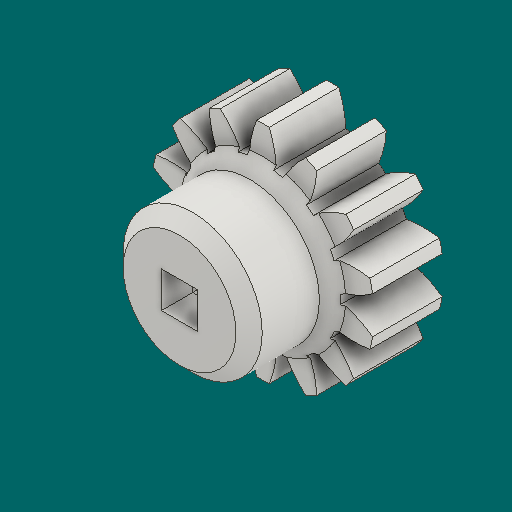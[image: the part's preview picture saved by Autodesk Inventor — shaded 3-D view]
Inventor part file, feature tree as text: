
AUTODESK INVENTOR PART (.ipt)
format: ipt  version: 2023.1 (Build 271208000, 208)  size: 332,800 bytes
history: native  units: in
note: dims shown in document units (in); Inventor stores cm internally (conversion verified against a paired STEP export)
features: other x12, sketch x5, plane x4
ambient origin geometry x8: Origin, YZ Plane, XZ Plane, XY Plane, X Axis, Y Axis, Z Axis, Center Point
bodies: Solid1 (feature_tree)
feature tree (21):
  other  "Spur Gear15_MIR.ipt"
  other  "Solid1::Spur Gear15_MIR.ipt"
  other  "TaggingFeature1"
  sketch  "Sketch1"  dims[d0=0.3937in]
  sketch  "Sketch2"  dims[d9=0.0in]
  sketch  "Sketch3"  dims[d14=0.0in]
  sketch  "Sketch4"  dims[d15=0.7in]
  sketch  "Sketch5"  dims[d16=0.0in d17=0.0in d18=0.0in d19=0.7in]
  plane  "XZ Plane_1"
  plane  "Work Plane2"
  plane  "Work Plane3"
  plane  "Work Plane4"
  other  "Srf1"
  other  "Srf1::Derived"
  other  "Start plane iMate"
  other  "Distance iMate"
  other  "Position iMate"
  other  "Mesh iMate"
  other  "Axis iMate"
  other  "Mesh iMate2"
  other  "Align iMate"
